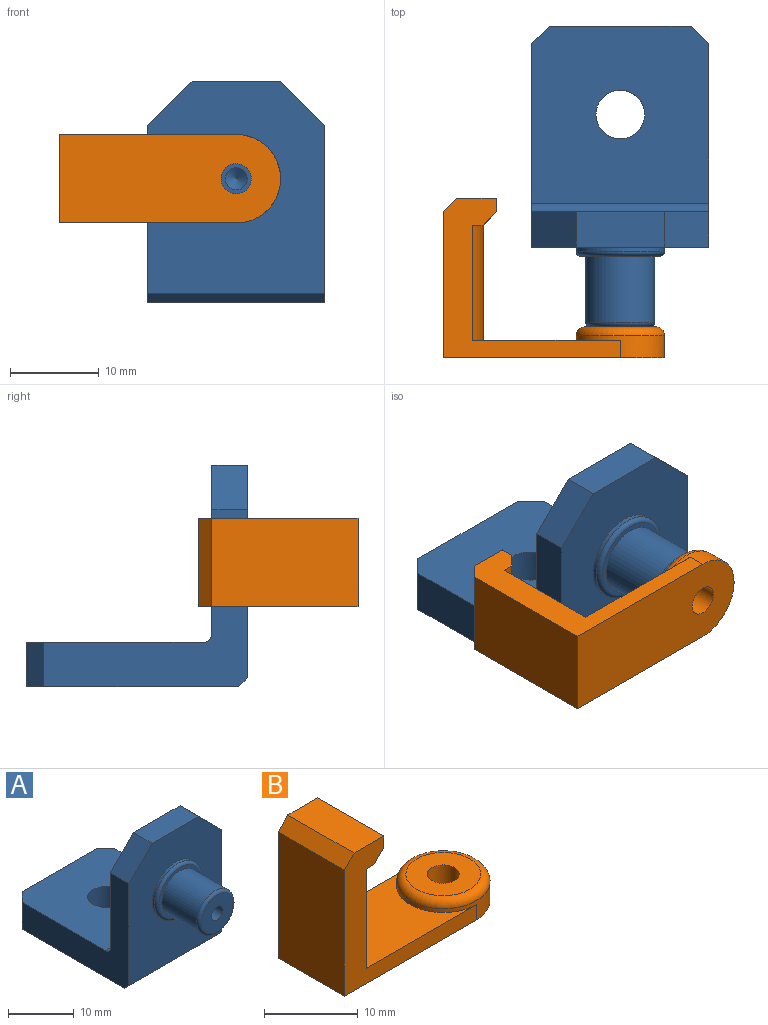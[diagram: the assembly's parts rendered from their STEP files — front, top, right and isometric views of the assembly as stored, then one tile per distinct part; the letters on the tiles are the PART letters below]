
ASSEMBLY  parts=2 mates=1
PART A: 23 faces, bbox 20x34x25 mm
  f0: plane 20x20mm, normal (0,0,1), area 372.2mm2, adj f1,f2,f4,f17,f18,f19,f20
  f1: plane 16x5mm, normal (0,1,0), area 80mm2, adj f0,f18,f19,f21
  f2: plane 23x20mm, normal (-1,0,0), area 174.7mm2, adj f0,f3,f5,f16,f18,f20,f21,f22
  f3: plane 24x20mm, normal (0,-1,0), area 376.5mm2, adj f2,f4,f6,f7,f15,f16,f22
  f4: plane 23x20mm, normal (1,0,0), area 174.7mm2, adj f0,f3,f5,f15,f19,f20,f21,f22
  f5: plane 20x19mm, normal (0,1,0), area 355mm2, adj f2,f4,f6,f15,f16,f20
  f6: plane 10x4mm, normal (0,0,1), area 40mm2, adj f3,f5,f15,f16
  f7: cylinder r=5mm len=10mm, axis (0,1,0), area 15.7mm2, adj f3,f14
  f8: plane 9x9mm, normal (0,-1,0), area 15.8mm2, adj f9,f14
  f9: cylinder r=3.9mm len=7.8mm, axis (0,1,0), area 183.8mm2, adj f8,f13
  f10: plane 6.8x6.8mm, normal (0,-1,0), area 31.4mm2, adj f12,f13
  f11: cone r=0mm half-angle=59deg, axis (0,-1,0), area 5.7mm2, adj f12
  f12: cylinder r=1.25mm len=8.5mm, axis (0,-1,0), area 66.8mm2, adj f10,f11
  f13: torus R=3.4mm, axis (0,-1,0), area 18.3mm2, adj f9,f10
  f14: torus R=4.5mm, axis (0,-1,0), area 23.8mm2, adj f7,f8
  f15: plane 5x5mm, normal (0.71,0,0.71), area 28.3mm2, adj f3,f4,f5,f6
  f16: plane 5x5mm, normal (-0.71,0,0.71), area 28.3mm2, adj f2,f3,f5,f6
  f17: cylinder r=2.75mm len=5.5mm, axis (0,0,-1), area 86.4mm2, adj f0,f21
  f18: plane 5x2mm, normal (-0.71,0.71,0), area 14.1mm2, adj f0,f1,f2,f21
  f19: plane 5x2mm, normal (0.71,0.71,0), area 14.1mm2, adj f0,f1,f4,f21
  f20: cylinder r=1mm len=20mm, axis (-1,0,0), area 31.4mm2, adj f0,f2,f4,f5
  f21: plane 24x20mm, normal (0,0,-1), area 452.2mm2, adj f1,f2,f4,f17,f18,f19,f22
  f22: plane 20x1mm, normal (0,-0.71,-0.71), area 28.3mm2, adj f2,f3,f4,f21
PART B: 16 faces, bbox 25.4x10.8x18 mm
  f0: plane 5x1.17mm, normal (0,0,-1), area 1.9mm2, adj f3,f9,f14
  f1: plane 25x10mm, normal (0,0,-1), area 230.2mm2, adj f3,f4,f5,f6,f10
  f2: plane 16.67x10mm, normal (0,0,1), area 119.6mm2, adj f3,f5,f6,f9
  f3: plane 20x18mm, normal (0,1,0), area 99mm2, adj f0,f1,f2,f4,f6,f9,f11,f12
  f4: plane 16.5x10mm, normal (-1,0,0), area 165mm2, adj f1,f3,f5,f15
  f5: plane 20x18mm, normal (0,-1,0), area 99mm2, adj f1,f2,f4,f6,f9,f11,f12,f13
  f6: cylinder r=5mm len=10mm, axis (0,0,-1), area 47.1mm2, adj f1,f2,f3,f5,f8
  f7: plane 8x8mm, normal (0,0,1), area 41.2mm2, adj f8,f10
  f8: torus R=4mm, axis (0,0,1), area 45.8mm2, adj f6,f7
  f9: cylinder r=11.25mm len=13mm, axis (0,0,-1), area 134.7mm2, adj f0,f2,f3,f5,f13
  f10: cylinder r=1.7mm len=3.5mm, axis (0,0,1), area 37.4mm2, adj f1,f7
  f11: plane 10x1.5mm, normal (1,0,0), area 15mm2, adj f3,f5,f12,f14
  f12: plane 10x4.5mm, normal (0,0,1), area 45mm2, adj f3,f5,f11,f15
  f13: plane 5x1.17mm, normal (0,0,-1), area 1.9mm2, adj f5,f9,f14
  f14: plane 10x1.5mm, normal (0.71,0,-0.71), area 21.2mm2, adj f0,f3,f5,f11,f13
  f15: plane 10x1.5mm, normal (-0.71,0,0.71), area 21.2mm2, adj f3,f4,f5,f12
PLACE A t=(-17.11,-5.92,-11.82)mm
PLACE B rot(axis=(-1,0,0),90deg) t=(-24.61,-30.92,-0.82)mm
MATE fastened B.f6 <-> A.f7  axis (0,1,0) through (-17.11,-27.42,-0.82)mm
